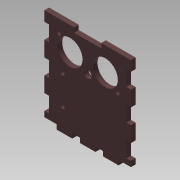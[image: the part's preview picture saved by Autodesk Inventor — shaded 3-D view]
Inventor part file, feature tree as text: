
AUTODESK INVENTOR PART (.ipt)
format: ipt  version: 2015 SP1 (Build 190203100, 203)  size: 152,064 bytes
history: native  units: mm
features: extrude x1, sketch x1
ambient origin geometry x8: Origin, YZ Plane, XZ Plane, XY Plane, X Axis, Y Axis, Z Axis, Center Point
bodies: Body1 (feature_tree)
feature tree (2):
  extrude  "Extrusion3"  Depth=20.0mm
  sketch  "Sketch1"  dims[d2=3.0mm d3=20.0mm d5=15.0mm d6=20.0mm d8=15.0mm d11=10.0mm d12=5.0mm d13=10.0mm d16=3.0mm d17=3.0mm d20=3.0mm d21=0.0mm]
